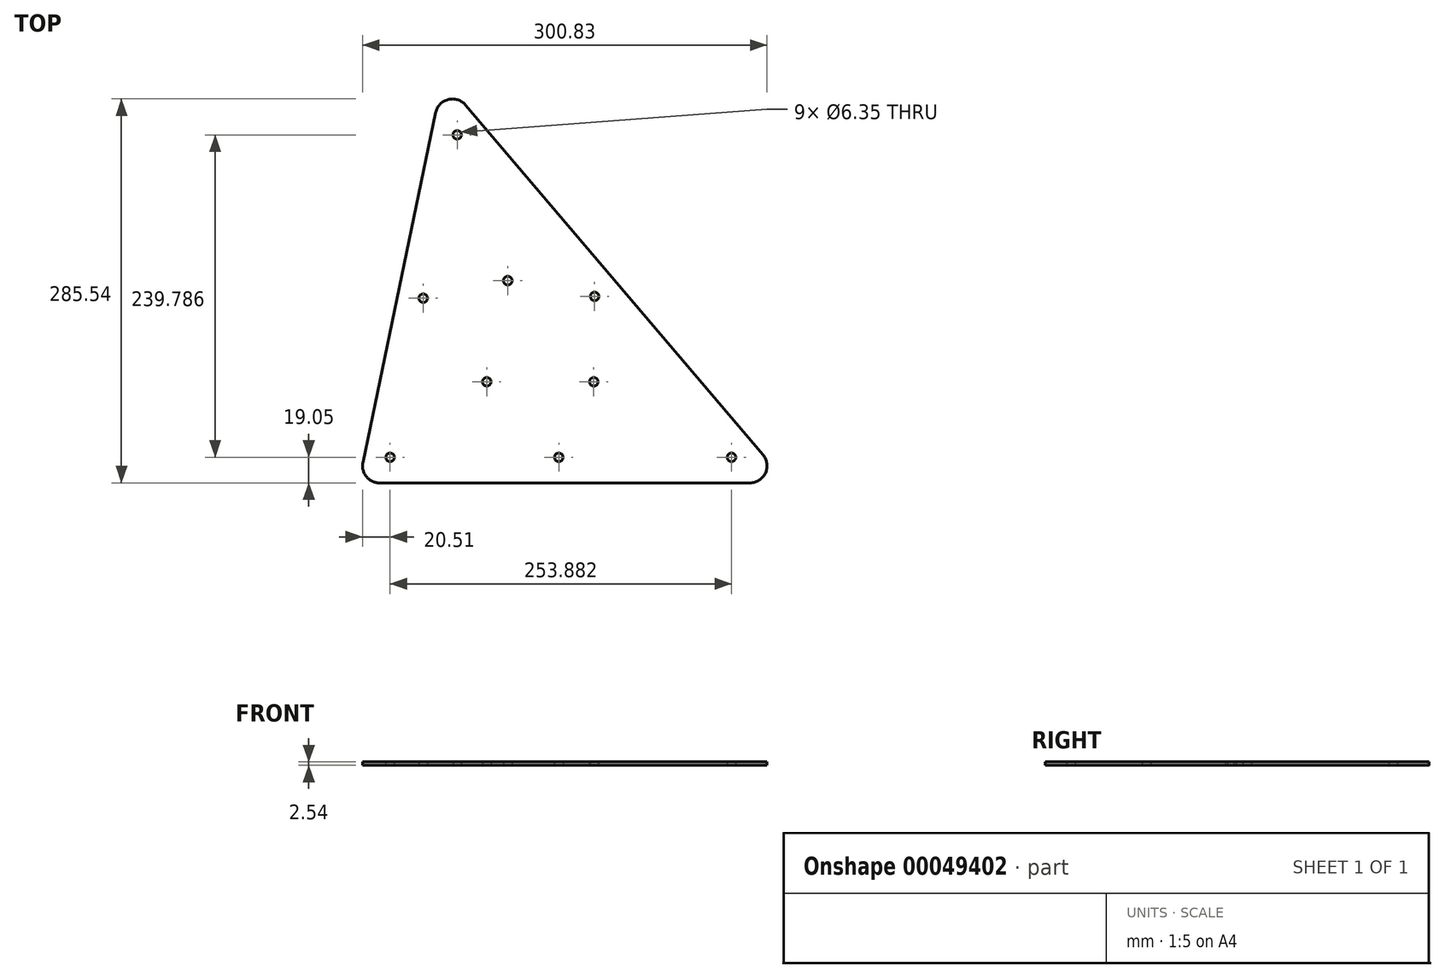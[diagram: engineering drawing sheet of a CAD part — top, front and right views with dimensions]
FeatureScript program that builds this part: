
annotation { "Feature Type Name" : "Feature", "Feature Type Description" : "" }
export const myFeature = defineFeature(function(context is Context, id is Id, definition is map)
    precondition{}
    {
        {
            var Q0;
            Q0=qCreatedBy(makeId("Top.planeOp"),FACE);
            var sketch = newSketch(context, id + "F0", { "sketchPlane" : qUnion([Q0])});
            skLineSegment(sketch, "E0", {"start": v(0, 0) * mm, "end": v(-255.94, 300.84) * mm});
            skLineSegment(sketch, "E1", {"start": v(-255.94, 300.84) * mm, "end": v(-318.52, 0) * mm});
            skLineSegment(sketch, "E2", {"start": v(-318.52, 0) * mm, "end": v(0, 0) * mm});
            skLineSegment(sketch, "E3", {"start": v(-287.23, 150.42) * mm, "end": v(-159.26, 0) * mm, "construction": true});
            skLineSegment(sketch, "E4", {"start": v(-159.26, 0) * mm, "end": v(-127.97, 150.42) * mm, "construction": true});
            skLineSegment(sketch, "E5", {"start": v(-127.97, 150.42) * mm, "end": v(-287.23, 150.42) * mm, "construction": true});
            skCircle(sketch, "E6", {"center": v(-295.1, 19.05) * mm, "radius": 3.18 * mm});
            skCircle(sketch, "E7", {"center": v(-41.22, 19.05) * mm, "radius": 3.18 * mm});
            skCircle(sketch, "E8", {"center": v(-245.22, 258.84) * mm, "radius": 3.18 * mm});
            skCircle(sketch, "E9", {"center": v(-207.6, 150.42) * mm, "radius": 3.18 * mm});
            skCircle(sketch, "E10", {"center": v(-143.62, 75.2) * mm, "radius": 3.18 * mm});
            skCircle(sketch, "E11", {"center": v(-223.25, 75.2) * mm, "radius": 3.18 * mm});
            skLineSegment(sketch, "E12", {"start": v(-159.26, 0) * mm, "end": v(-207.6, 88.52) * mm, "construction": true});
            skLineSegment(sketch, "E13", {"start": v(-207.6, 88.52) * mm, "end": v(-287.23, 150.42) * mm, "construction": true});
            skLineSegment(sketch, "E14", {"start": v(-207.6, 88.52) * mm, "end": v(-127.97, 150.42) * mm, "construction": true});
            skCircle(sketch, "E15", {"center": v(-270.48, 137.4) * mm, "radius": 3.18 * mm});
            skCircle(sketch, "E16", {"center": v(-143.02, 138.72) * mm, "radius": 3.18 * mm});
            skCircle(sketch, "E17", {"center": v(-169.66, 19.05) * mm, "radius": 3.18 * mm});
            skSolve(sketch);
        }
        {
            var Q0;
            Q0 = qSketchRegion(id + "F0", true);
            extrude(context, id + "F1", {"entities" : qUnion([Q0]), "depth" : 2.54 * mm});
        }
        {
            var Q0;
            Q0=makeQuery(id+"F1.opExtrude","SWEPT_EDGE",EDGE,{"disambiguationData":[OSD([sQuery(id+"F0.wireOp",EDGE,"E1"),sQuery(id+"F0.wireOp",EDGE,"E2")])]});
            var Q1;
            Q1=makeQuery(id+"F1.opExtrude","SWEPT_EDGE",EDGE,{"disambiguationData":[OSD([sQuery(id+"F0.wireOp",EDGE,"E0"),sQuery(id+"F0.wireOp",EDGE,"E2")])]});
            var Q2;
            Q2=makeQuery(id+"F1.opExtrude","SWEPT_EDGE",EDGE,{"disambiguationData":[OSD([sQuery(id+"F0.wireOp",EDGE,"E0"),sQuery(id+"F0.wireOp",EDGE,"E1")])]});
            fillet(context, id + "F2", {"entities" : qUnion([Q0, Q1, Q2]), "radius" : 12.7 * mm, "tangentPropagation" : true, "allowEdgeOverflow" : false});
        }
    });
